# Revit family: LA2-QUAD
name_source: partatom
category: Lighting Fixtures
revit_build: Autodesk Revit 2014 (Build: 20140709_2115(x64)
units: mm (PartAtom-declared; Revit-internal decimal feet)

## types (1)
- 46"L x 46"W x 4"H
    16 = Yes
    Adjustable Suspension Height = 4' - 0"
    Cables = (4)3/64" stainless steel cables
    Canopy Type = la2-connect
    Color Filter = 16777215
    Diffuser = White Opal Acrylic
    Dimming Compatibility = 0-10v
    Dimming Lamp Color Temperature Shift = <None>
    Hardware = Stainless Steel Cables
    Height = 0' - 4"
    Input = 120v-277v
    Intensity = LED System
    Length = 3' - 10"
    Lid = Removable powder coated
    Light Source Symbol Size = 0' - 8"
    Manufacturer = LightArt
    Material Options = http://www.3-form.com
    Model = QUAD
    Shade = 3form Varia Ecoresin
    Standards = 6-8 week lead time
    Type Comments = Does not include lamp
    URL = http://lightart.com
    Wattage Comments = 14
    Width = 3' - 10"

## geometry (parser evidence)
native form markers: Sweep x26
no freeform markers — native parametric forms only
